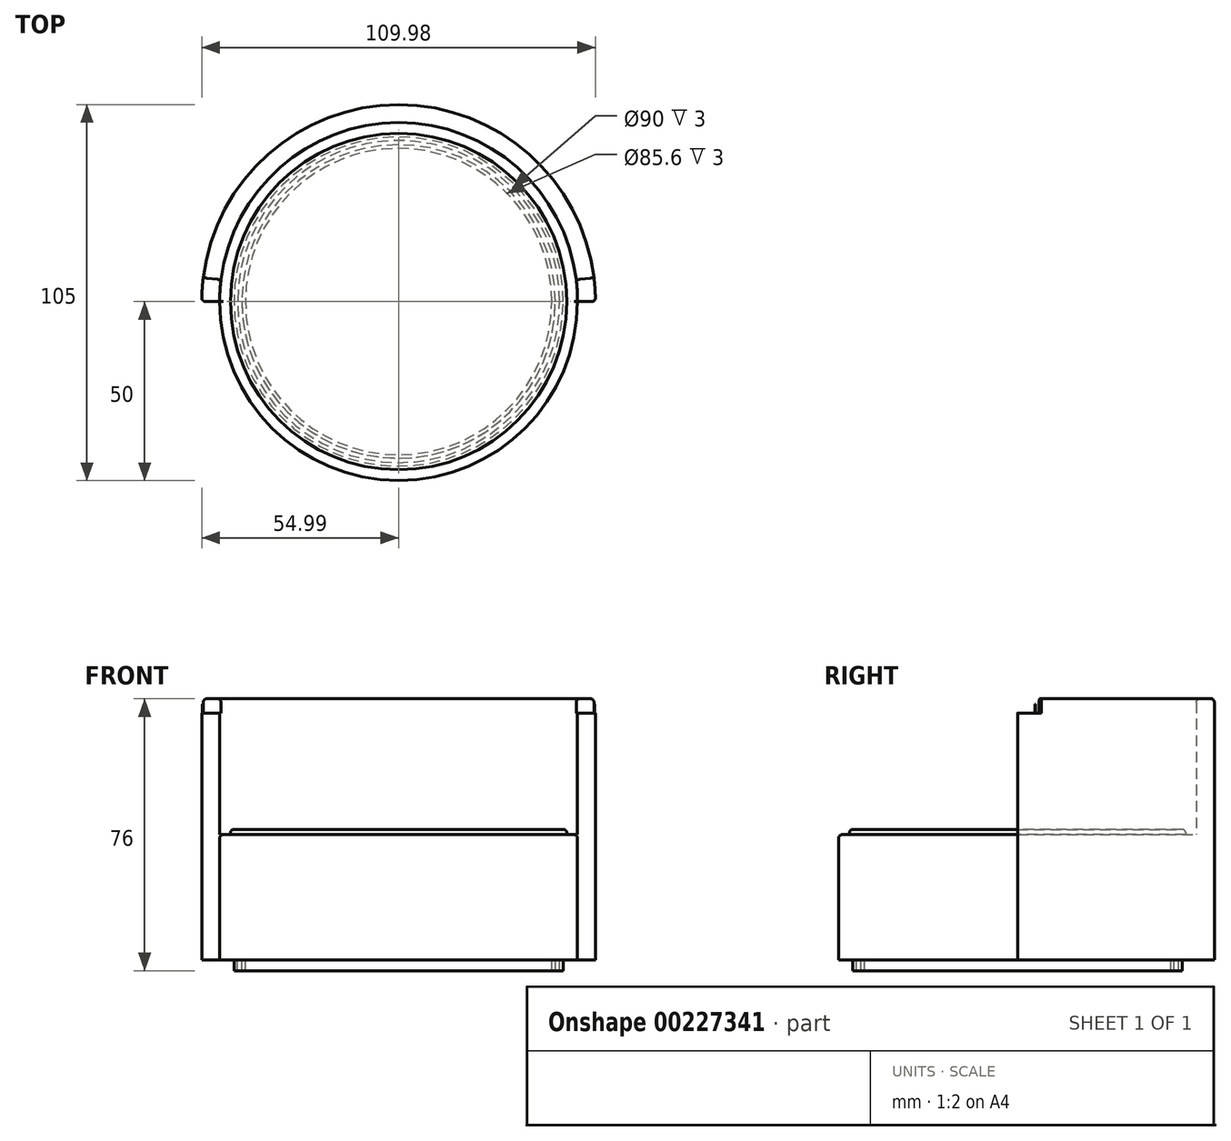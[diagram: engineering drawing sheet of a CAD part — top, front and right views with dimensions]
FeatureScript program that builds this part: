
annotation { "Feature Type Name" : "Feature", "Feature Type Description" : "" }
export const myFeature = defineFeature(function(context is Context, id is Id, definition is map)
    precondition{}
    {
        {
            var Q0;
            Q0=qCreatedBy(makeId("Top.planeOp"),FACE);
            var sketch = newSketch(context, id + "F0", { "sketchPlane" : qUnion([Q0])});
            skCircle(sketch, "E0", {"center": v(0, 0) * mm, "radius": 50 * mm});
            skArc(sketch, "E1", {"start": v(55, 0) * mm, "mid": v(0, 55) * mm, "end": v(-55, 0) * mm});
            skLineSegment(sketch, "E2", {"start": v(-55, 0) * mm, "end": v(-50, 0) * mm});
            skLineSegment(sketch, "E3", {"start": v(55, 0) * mm, "end": v(50, 0) * mm});
            skSolve(sketch);
        }
        {
            var Q0;
            Q0=makeQuery(id+"F0.imprint","IMPRINT",FACE,{"disambiguationData":[TD([[makeQuery(id+"F0.imprint","IMPRINT",EDGE,{"derivedFrom":sQuery(id+"F0.wireOp",EDGE,"E0")}),1.0]])]});
            var sketch = newSketch(context, id + "F1", { "sketchPlane" : qUnion([Q0])});
            skCircle(sketch, "E4.0", {"center": v(0, 0) * mm, "radius": 46 * mm});
            skCircle(sketch, "E5.0", {"center": v(0, 0) * mm, "radius": 45 * mm});
            skSolve(sketch);
        }
        {
            var Q0;
            Q0=makeQuery(id+"F0.imprint","IMPRINT",FACE,{"disambiguationData":[TD([[makeQuery(id+"F0.imprint","IMPRINT",EDGE,{"derivedFrom":sQuery(id+"F0.wireOp",EDGE,"E0")}),1.0]])]});
            var sketch = newSketch(context, id + "F2", { "sketchPlane" : qUnion([Q0])});
            skCircle(sketch, "E6.0", {"center": v(0, 0) * mm, "radius": 43.8 * mm});
            skCircle(sketch, "E7.0", {"center": v(0, 0) * mm, "radius": 42.8 * mm});
            skSolve(sketch);
        }
        {
            var Q0;
            Q0=makeQuery(id+"F2.imprint","IMPRINT",FACE,{"disambiguationData":[TD([[makeQuery(id+"F2.imprint","IMPRINT",EDGE,{"derivedFrom":sQuery(id+"F2.wireOp",EDGE,"E6.0")}),1.0]])]});
            extrude(context, id + "F3", {"entities" : qUnion([Q0]), "oppositeDirection" : true, "depth" : 1.5 * mm});
        }
        {
            var Q0;
            Q0 = qSketchRegion(id + "F1", true);
            extrude(context, id + "F4", {"entities" : qUnion([Q0]), "oppositeDirection" : true, "depth" : 1.5 * mm});
        }
        {
            var Q0;
            Q0 = qSketchRegion(id + "F0", true);
            extrude(context, id + "F5", {"entities" : qUnion([Q0]), "depth" : 35 * mm});
        }
        {
            var Q0;
            Q0=makeQuery(id+"F5.opExtrude","CAP_FACE",FACE,{"disambiguationData":[OSD([sQuery(id+"F0.wireOp",EDGE,"E0"),sQuery(id+"F0.wireOp",EDGE,"E1"),sQuery(id+"F0.wireOp",EDGE,"E2"),sQuery(id+"F0.wireOp",EDGE,"E3")])],"isStart":false});
            var sketch = newSketch(context, id + "F6", { "sketchPlane" : qUnion([Q0])});
            skArc(sketch, "E8", {"start": v(50, 0) * mm, "mid": v(0, 50) * mm, "end": v(-50, 0) * mm});
            skSolve(sketch);
        }
        {
            var Q0;
            Q0=makeQuery(id+"F6.imprint","IMPRINT",FACE,{"disambiguationData":[TD([[makeQuery(id+"F6.imprint","IMPRINT",EDGE,{"derivedFrom":sQuery(id+"F6.wireOp",EDGE,"E8")}),-1.0]])]});
            extrude(context, id + "F7", {"entities" : qUnion([Q0]), "operationType" : NewBodyOperationType.ADD, "depth" : 34 * mm});
        }
        {
            var Q0;
            Q0=makeQuery(id+"F5.opExtrude","CAP_FACE",FACE,{"disambiguationData":[OSD([sQuery(id+"F0.wireOp",EDGE,"E0"),sQuery(id+"F0.wireOp",EDGE,"E1"),sQuery(id+"F0.wireOp",EDGE,"E2"),sQuery(id+"F0.wireOp",EDGE,"E3")])],"isStart":false});
            var sketch = newSketch(context, id + "F8", { "sketchPlane" : qUnion([Q0])});
            skArc(sketch, "E9.0", {"start": v(-47, 0) * mm, "mid": v(0, -47) * mm, "end": v(47, 0) * mm});
            skArc(sketch, "E9.1", {"start": v(47, 0) * mm, "mid": v(0, 47) * mm, "end": v(-47, 0) * mm});
            skSolve(sketch);
        }
        {
            var Q0;
            Q0=makeQuery(id+"F8.imprint","IMPRINT",FACE,{"disambiguationData":[TD([[makeQuery(id+"F8.imprint","IMPRINT",EDGE,{"derivedFrom":sQuery(id+"F8.wireOp",EDGE,"E9.0")}),1.0]])]});
            extrude(context, id + "F9", {"entities" : qUnion([Q0]), "operationType" : NewBodyOperationType.ADD, "depth" : 1.5 * mm});
        }
        {
            var Q0;
            Q0=makeQuery(id+"F3.opExtrude","SWEPT_BODY",BODY,{"disambiguationData":[OSD([sQuery(id+"F2.wireOp",EDGE,"E6.0"),sQuery(id+"F2.wireOp",EDGE,"E7.0")])]});
            deleteBodies(context, id + "F10", {"entities" : qUnion([Q0])});
        }
        {
            var Q0;
            Q0=makeQuery(id+"F4.opExtrude","SWEPT_BODY",BODY,{"disambiguationData":[OSD([sQuery(id+"F1.wireOp",EDGE,"E4.0"),sQuery(id+"F1.wireOp",EDGE,"E5.0")])]});
            deleteBodies(context, id + "F11", {"entities" : qUnion([Q0])});
        }
        {
            var Q0;
            Q0=makeQuery(id+"F5.opExtrude","CAP_FACE",FACE,{"disambiguationData":[OSD([sQuery(id+"F0.wireOp",EDGE,"E0"),sQuery(id+"F0.wireOp",EDGE,"E1"),sQuery(id+"F0.wireOp",EDGE,"E2"),sQuery(id+"F0.wireOp",EDGE,"E3")])],"isStart":true});
            var sketch = newSketch(context, id + "F12", { "sketchPlane" : qUnion([Q0])});
            skCircle(sketch, "E10", {"center": v(0, 0) * mm, "radius": 45 * mm});
            skCircle(sketch, "E11.0", {"center": v(0, 0) * mm, "radius": 46 * mm});
            skCircle(sketch, "E12.0", {"center": v(0, 0) * mm, "radius": 43.8 * mm});
            skCircle(sketch, "E13.0", {"center": v(0, 0) * mm, "radius": 42.8 * mm});
            skSolve(sketch);
        }
        {
            var Q0;
            Q0=makeQuery(id+"F12.imprint","IMPRINT",FACE,{"disambiguationData":[TD([[makeQuery(id+"F12.imprint","IMPRINT",EDGE,{"derivedFrom":sQuery(id+"F12.wireOp",EDGE,"E10")}),-1.0]])]});
            extrude(context, id + "F13", {"entities" : qUnion([Q0]), "operationType" : NewBodyOperationType.ADD, "depth" : 3 * mm});
        }
        {
            var Q0;
            Q0=makeQuery(id+"F12.imprint","IMPRINT",FACE,{"disambiguationData":[TD([[makeQuery(id+"F12.imprint","IMPRINT",EDGE,{"derivedFrom":sQuery(id+"F12.wireOp",EDGE,"E12.0")}),1.0]])]});
            extrude(context, id + "F14", {"entities" : qUnion([Q0]), "operationType" : NewBodyOperationType.ADD, "depth" : 3 * mm});
        }
        {
            var Q0;
            Q0=makeQuery(id+"F7.opExtrude","CAP_FACE",FACE,{"disambiguationData":[OSD([sQuery(id+"F0.wireOp",EDGE,"E1"),sQuery(id+"F0.wireOp",EDGE,"E2"),sQuery(id+"F0.wireOp",EDGE,"E3"),sQuery(id+"F6.wireOp",EDGE,"E8")])],"isStart":false});
            var sketch = newSketch(context, id + "F15", { "sketchPlane" : qUnion([Q0])});
            skLineSegment(sketch, "E14", {"start": v(-49.8, 4.5) * mm, "end": v(-54.78, 4.95) * mm});
            skLineSegment(sketch, "E15", {"start": v(-54.78, 4.95) * mm, "end": v(-55, 0) * mm});
            skLineSegment(sketch, "E16", {"start": v(-55, 0) * mm, "end": v(-50, 0) * mm});
            skLineSegment(sketch, "E17", {"start": v(-50, 0) * mm, "end": v(-49.8, 4.5) * mm});
            skLineSegment(sketch, "E18", {"start": v(-54.6, 6.67) * mm, "end": v(-49.63, 6.07) * mm});
            skLineSegment(sketch, "E19", {"start": v(-54.6, 6.67) * mm, "end": v(-54.78, 4.95) * mm});
            skLineSegment(sketch, "E20", {"start": v(-49.63, 6.07) * mm, "end": v(-49.8, 4.5) * mm});
            skLineSegment(sketch, "E21.MirrorCS", {"start": v(54.6, 6.67) * mm, "end": v(49.63, 6.07) * mm});
            skLineSegment(sketch, "E22.MirrorCS", {"start": v(49.8, 4.5) * mm, "end": v(54.78, 4.95) * mm});
            skLineSegment(sketch, "E23.MirrorCS", {"start": v(54.78, 4.95) * mm, "end": v(55, 0) * mm});
            skLineSegment(sketch, "E24.MirrorCS", {"start": v(50, 0) * mm, "end": v(49.8, 4.5) * mm});
            skLineSegment(sketch, "E25.MirrorCS", {"start": v(55, 0) * mm, "end": v(50, 0) * mm});
            skLineSegment(sketch, "E26.MirrorCS", {"start": v(54.6, 6.67) * mm, "end": v(54.78, 4.95) * mm});
            skLineSegment(sketch, "E27.MirrorCS", {"start": v(49.63, 6.07) * mm, "end": v(49.8, 4.5) * mm});
            skSolve(sketch);
        }
        {
            var Q0;
            {var subQ0=sQuery(id+"F15.wireOp",EDGE,"E18");Q0=makeQuery(id+"F15.imprint","IMPRINT",FACE,{"disambiguationData":[TD([[makeQuery(id+"F15.imprint","IMPRINT",EDGE,{"derivedFrom":subQ0}),1.0]])]});}
            extrude(context, id + "F16", {"entities" : qUnion([Q0]), "operationType" : NewBodyOperationType.ADD, "depth" : 4 * mm});
        }
        {
            var Q0;
            {var subQ0=sQuery(id+"F15.wireOp",EDGE,"E14");Q0=makeQuery(id+"F15.imprint","IMPRINT",FACE,{"disambiguationData":[TD([[makeQuery(id+"F15.imprint","IMPRINT",EDGE,{"derivedFrom":subQ0}),1.0]])]});}
            var Q1;
            {var subQ0=sQuery(id+"F15.wireOp",EDGE,"E22.MirrorCS");Q1=makeQuery(id+"F15.imprint","IMPRINT",FACE,{"disambiguationData":[TD([[makeQuery(id+"F15.imprint","IMPRINT",EDGE,{"derivedFrom":subQ0}),-1.0]])]});}
            extrude(context, id + "F17", {"entities" : qUnion([Q0, Q1]), "operationType" : NewBodyOperationType.ADD, "depth" : 2.5 * mm});
        }
        {
            var Q0;
            Q0=makeQuery(id+"F16.opExtrude","CAP_EDGE",EDGE,{"disambiguationData":[OSD([sQuery(id+"F6.wireOp",EDGE,"E8")])],"isStart":false});
            var Q1;
            {var subQ0=sQuery(id+"F0.wireOp",EDGE,"E2");var subQ1=sQuery(id+"F0.wireOp",EDGE,"E1");Q1=makeQuery(id+"F7.boolean.opBoolean","MERGE",EDGE,{"derivedFrom":[makeQuery(id+"F5.opExtrude","SWEPT_EDGE",EDGE,{"disambiguationData":[OSD([subQ1,subQ0])]}),makeQuery(id+"F7.opExtrude","SWEPT_EDGE",EDGE,{"disambiguationData":[OSD([subQ1,subQ0])]})]});}
            var Q2;
            Q2=makeQuery(id+"F16.opExtrude","CAP_EDGE",EDGE,{"disambiguationData":[OSD([sQuery(id+"F0.wireOp",EDGE,"E1")])],"isStart":false});
            var Q3;
            {var subQ0=sQuery(id+"F0.wireOp",EDGE,"E3");var subQ1=sQuery(id+"F0.wireOp",EDGE,"E1");Q3=makeQuery(id+"F7.boolean.opBoolean","MERGE",EDGE,{"derivedFrom":[makeQuery(id+"F5.opExtrude","SWEPT_EDGE",EDGE,{"disambiguationData":[OSD([subQ1,subQ0])]}),makeQuery(id+"F7.opExtrude","SWEPT_EDGE",EDGE,{"disambiguationData":[OSD([subQ1,subQ0])]})]});}
            var Q4;
            Q4=makeQuery(id+"F9.opExtrude","CAP_EDGE",EDGE,{"disambiguationData":[OSD([sQuery(id+"F8.wireOp",EDGE,"E9.0"),sQuery(id+"F8.wireOp",EDGE,"E9.1")])],"isStart":false});
            var Q5;
            Q5=makeQuery(id+"F5.opExtrude","CAP_EDGE",EDGE,{"disambiguationData":[OSD([sQuery(id+"F0.wireOp",EDGE,"E0")])],"isStart":false});
            fillet(context, id + "F18", {"entities" : qUnion([Q0, Q1, Q2, Q3, Q4, Q5]), "radius" : 1 * mm, "tangentPropagation" : true, "allowEdgeOverflow" : false});
        }
    });
